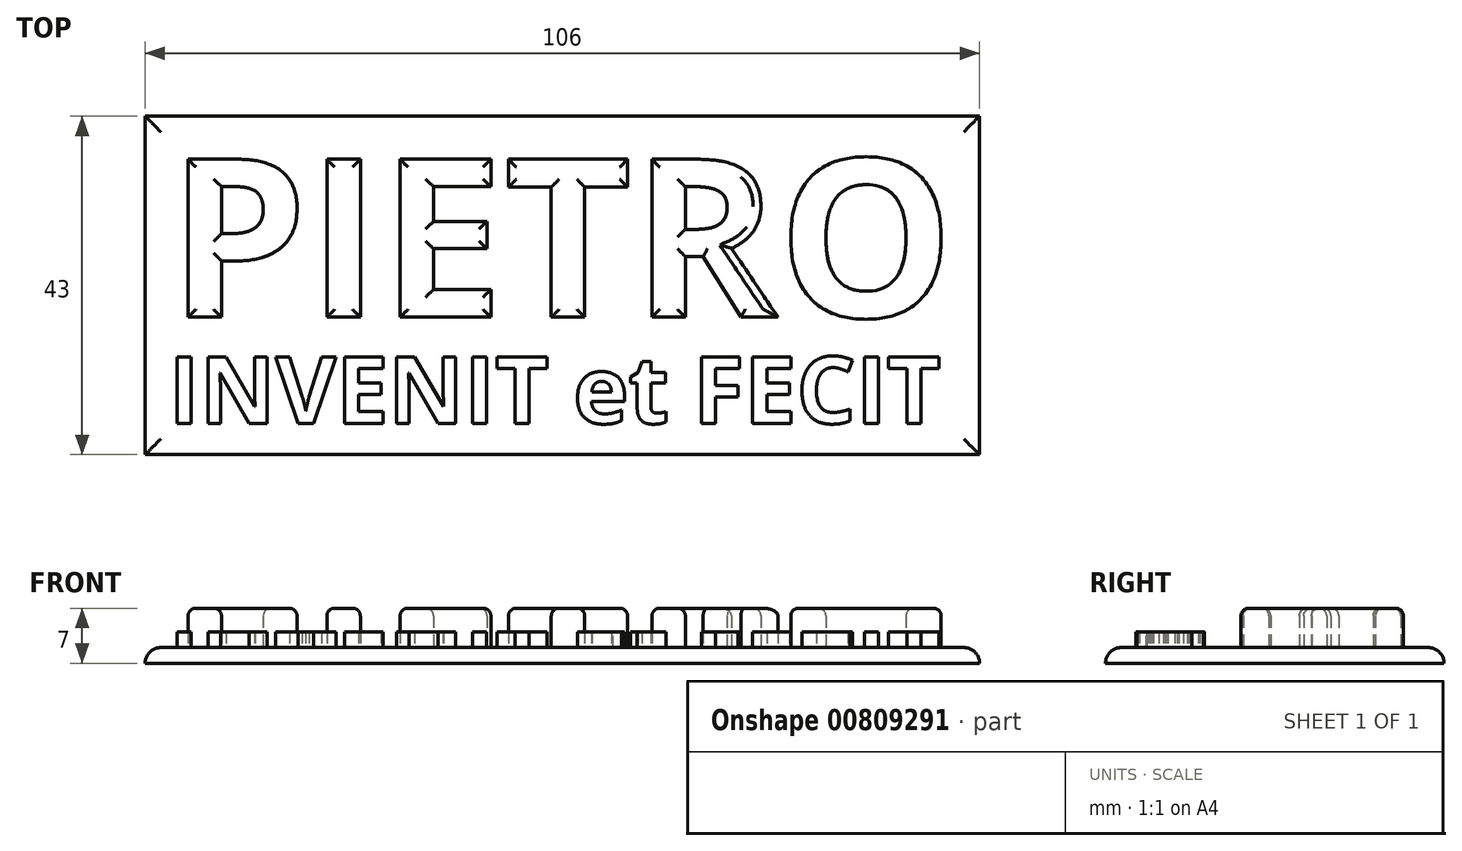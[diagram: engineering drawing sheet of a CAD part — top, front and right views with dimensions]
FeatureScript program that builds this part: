
annotation { "Feature Type Name" : "Feature", "Feature Type Description" : "" }
export const myFeature = defineFeature(function(context is Context, id is Id, definition is map)
    precondition{}
    {
        {
            var Q0;
            Q0=qCreatedBy(makeId("Top.planeOp"),FACE);
            var sketch = newSketch(context, id + "F0", { "sketchPlane" : qUnion([Q0])});
            skText(sketch, "E0", { "text": "PIETRO", "fontName": "OpenSans-Bold.ttf"});
            skText(sketch, "E1", { "text": "INVENIT et FECIT", "fontName": "OpenSans-Bold.ttf"});
            const initialGuessF0  = {"E0": [-0.02736, -0.01022, 1, 0, 0.02022], "E1": [-0.02728, -0.02372, 1, 0, 0.00853]};
            skSetInitialGuess(sketch, initialGuessF0);
            skSolve(sketch);
        }
        {
            var Q0;
            Q0=qCreatedBy(makeId("Top.planeOp"),FACE);
            var sketch = newSketch(context, id + "F1", { "sketchPlane" : qUnion([Q0])});
            skLineSegment(sketch, "E2.bottom", {"start": v(-30.29, 15.3) * mm, "end": v(75.71, 15.3) * mm});
            skLineSegment(sketch, "E2.top", {"start": v(-30.29, -27.7) * mm, "end": v(75.71, -27.7) * mm});
            skLineSegment(sketch, "E2.left", {"start": v(-30.29, 15.3) * mm, "end": v(-30.29, -27.7) * mm});
            skLineSegment(sketch, "E2.right", {"start": v(75.71, 15.3) * mm, "end": v(75.71, -27.7) * mm});
            skSolve(sketch);
        }
        {
            var Q0;
            Q0=makeQuery(id+"F1.imprint","IMPRINT",FACE,{"disambiguationData":[TD([[makeQuery(id+"F1.imprint","IMPRINT",EDGE,{"derivedFrom":sQuery(id+"F1.wireOp",EDGE,"E2.bottom")}),-1.0]])]});
            extrude(context, id + "F2", {"entities" : qUnion([Q0]), "depth" : -2 * mm, "offsetDistance" : 25 * mm});
        }
        {
            var Q0;
            Q0=makeQuery(id+"F0.imprint","IMPRINT",FACE,{"disambiguationData":[TD([[makeQuery(id+"F0.imprint","IMPRINT",EDGE,{"derivedFrom":sQuery(id+"F0.wireOp",EDGE,"E0.sketch_text.stroke-0")}),-1.0]])]});
            var Q1;
            Q1=makeQuery(id+"F0.imprint","IMPRINT",FACE,{"disambiguationData":[TD([[makeQuery(id+"F0.imprint","IMPRINT",EDGE,{"derivedFrom":sQuery(id+"F0.wireOp",EDGE,"E0.sketch_text.stroke-16")}),-1.0]])]});
            var Q2;
            Q2=makeQuery(id+"F0.imprint","IMPRINT",FACE,{"disambiguationData":[TD([[makeQuery(id+"F0.imprint","IMPRINT",EDGE,{"derivedFrom":sQuery(id+"F0.wireOp",EDGE,"E0.sketch_text.stroke-20")}),-1.0]])]});
            var Q3;
            Q3=makeQuery(id+"F0.imprint","IMPRINT",FACE,{"disambiguationData":[TD([[makeQuery(id+"F0.imprint","IMPRINT",EDGE,{"derivedFrom":sQuery(id+"F0.wireOp",EDGE,"E0.sketch_text.stroke-32")}),-1.0]])]});
            var Q4;
            Q4=makeQuery(id+"F0.imprint","IMPRINT",FACE,{"disambiguationData":[TD([[makeQuery(id+"F0.imprint","IMPRINT",EDGE,{"derivedFrom":sQuery(id+"F0.wireOp",EDGE,"E0.sketch_text.stroke-40")}),-1.0]])]});
            var Q5;
            Q5=makeQuery(id+"F0.imprint","IMPRINT",FACE,{"disambiguationData":[TD([[makeQuery(id+"F0.imprint","IMPRINT",EDGE,{"derivedFrom":sQuery(id+"F0.wireOp",EDGE,"E0.sketch_text.stroke-59")}),-1.0]])]});
            extrude(context, id + "F3", {"entities" : qUnion([Q0, Q1, Q2, Q3, Q4, Q5]), "operationType" : NewBodyOperationType.ADD, "depth" : 5 * mm, "offsetDistance" : 25 * mm});
        }
        {
            var Q0;
            Q0=makeQuery(id+"F0.imprint","IMPRINT",FACE,{"disambiguationData":[TD([[makeQuery(id+"F0.imprint","IMPRINT",EDGE,{"derivedFrom":sQuery(id+"F0.wireOp",EDGE,"E1.sketch_text.stroke-0")}),-1.0]])]});
            var Q1;
            Q1=makeQuery(id+"F0.imprint","IMPRINT",FACE,{"disambiguationData":[TD([[makeQuery(id+"F0.imprint","IMPRINT",EDGE,{"derivedFrom":sQuery(id+"F0.wireOp",EDGE,"E1.sketch_text.stroke-4")}),-1.0]])]});
            var Q2;
            Q2=makeQuery(id+"F0.imprint","IMPRINT",FACE,{"disambiguationData":[TD([[makeQuery(id+"F0.imprint","IMPRINT",EDGE,{"derivedFrom":sQuery(id+"F0.wireOp",EDGE,"E1.sketch_text.stroke-18")}),-1.0]])]});
            var Q3;
            Q3=makeQuery(id+"F0.imprint","IMPRINT",FACE,{"disambiguationData":[TD([[makeQuery(id+"F0.imprint","IMPRINT",EDGE,{"derivedFrom":sQuery(id+"F0.wireOp",EDGE,"E1.sketch_text.stroke-28")}),-1.0]])]});
            var Q4;
            Q4=makeQuery(id+"F0.imprint","IMPRINT",FACE,{"disambiguationData":[TD([[makeQuery(id+"F0.imprint","IMPRINT",EDGE,{"derivedFrom":sQuery(id+"F0.wireOp",EDGE,"E1.sketch_text.stroke-40")}),-1.0]])]});
            var Q5;
            Q5=makeQuery(id+"F0.imprint","IMPRINT",FACE,{"disambiguationData":[TD([[makeQuery(id+"F0.imprint","IMPRINT",EDGE,{"derivedFrom":sQuery(id+"F0.wireOp",EDGE,"E1.sketch_text.stroke-54")}),-1.0]])]});
            var Q6;
            Q6=makeQuery(id+"F0.imprint","IMPRINT",FACE,{"disambiguationData":[TD([[makeQuery(id+"F0.imprint","IMPRINT",EDGE,{"derivedFrom":sQuery(id+"F0.wireOp",EDGE,"E1.sketch_text.stroke-58")}),-1.0]])]});
            var Q7;
            Q7=makeQuery(id+"F0.imprint","IMPRINT",FACE,{"disambiguationData":[TD([[makeQuery(id+"F0.imprint","IMPRINT",EDGE,{"derivedFrom":sQuery(id+"F0.wireOp",EDGE,"E1.sketch_text.stroke-66")}),-1.0]])]});
            var Q8;
            Q8=makeQuery(id+"F0.imprint","IMPRINT",FACE,{"disambiguationData":[TD([[makeQuery(id+"F0.imprint","IMPRINT",EDGE,{"derivedFrom":sQuery(id+"F0.wireOp",EDGE,"E1.sketch_text.stroke-78")}),-1.0]])]});
            var Q9;
            Q9=makeQuery(id+"F0.imprint","IMPRINT",FACE,{"disambiguationData":[TD([[makeQuery(id+"F0.imprint","IMPRINT",EDGE,{"derivedFrom":sQuery(id+"F0.wireOp",EDGE,"E1.sketch_text.stroke-86")}),-1.0]])]});
            var Q10;
            Q10=makeQuery(id+"F0.imprint","IMPRINT",FACE,{"disambiguationData":[TD([[makeQuery(id+"F0.imprint","IMPRINT",EDGE,{"derivedFrom":sQuery(id+"F0.wireOp",EDGE,"E1.sketch_text.stroke-96")}),-1.0]])]});
            var Q11;
            Q11=makeQuery(id+"F0.imprint","IMPRINT",FACE,{"disambiguationData":[TD([[makeQuery(id+"F0.imprint","IMPRINT",EDGE,{"derivedFrom":sQuery(id+"F0.wireOp",EDGE,"E1.sketch_text.stroke-108")}),-1.0]])]});
            var Q12;
            Q12=makeQuery(id+"F0.imprint","IMPRINT",FACE,{"disambiguationData":[TD([[makeQuery(id+"F0.imprint","IMPRINT",EDGE,{"derivedFrom":sQuery(id+"F0.wireOp",EDGE,"E1.sketch_text.stroke-123")}),-1.0]])]});
            var Q13;
            Q13=makeQuery(id+"F0.imprint","IMPRINT",FACE,{"disambiguationData":[TD([[makeQuery(id+"F0.imprint","IMPRINT",EDGE,{"derivedFrom":sQuery(id+"F0.wireOp",EDGE,"E1.sketch_text.stroke-127")}),-1.0]])]});
            var Q14;
            Q14=makeQuery(id+"F0.imprint","IMPRINT",FACE,{"disambiguationData":[TD([[makeQuery(id+"F0.imprint","IMPRINT",EDGE,{"derivedFrom":sQuery(id+"F0.wireOp",EDGE,"E1.sketch_text.stroke-141")}),-1.0]])]});
            var Q15;
            Q15=makeQuery(id+"F0.imprint","IMPRINT",FACE,{"disambiguationData":[TD([[makeQuery(id+"F0.imprint","IMPRINT",EDGE,{"derivedFrom":sQuery(id+"F0.wireOp",EDGE,"E1.sketch_text.stroke-145")}),-1.0]])]});
            extrude(context, id + "F4", {"entities" : qUnion([Q0, Q1, Q2, Q3, Q4, Q5, Q6, Q7, Q8, Q9, Q10, Q11, Q12, Q13, Q14, Q15]), "operationType" : NewBodyOperationType.ADD, "depth" : 2 * mm, "offsetDistance" : 25 * mm});
        }
        {
            var Q0;
            Q0=makeQuery(id+"F2.opExtrude","CAP_EDGE",EDGE,{"disambiguationData":[OSD([sQuery(id+"F1.wireOp",EDGE,"E2.right")])],"isStart":true});
            var Q1;
            Q1=makeQuery(id+"F2.opExtrude","CAP_EDGE",EDGE,{"disambiguationData":[OSD([sQuery(id+"F1.wireOp",EDGE,"E2.bottom")])],"isStart":true});
            var Q2;
            Q2=makeQuery(id+"F2.opExtrude","CAP_EDGE",EDGE,{"disambiguationData":[OSD([sQuery(id+"F1.wireOp",EDGE,"E2.top")])],"isStart":true});
            var Q3;
            Q3=makeQuery(id+"F2.opExtrude","CAP_EDGE",EDGE,{"disambiguationData":[OSD([sQuery(id+"F1.wireOp",EDGE,"E2.left")])],"isStart":true});
            fillet(context, id + "F5", {"entities" : qUnion([Q0, Q1, Q2, Q3]), "radius" : 2 * mm, "tangentPropagation" : true, "allowEdgeOverflow" : false});
        }
        {
            var Q0;
            Q0=makeQuery(id+"F3.opExtrude","CAP_FACE",FACE,{"disambiguationData":[OSD([sQuery(id+"F0.wireOp",EDGE,"E0.sketch_text.stroke-0"),sQuery(id+"F0.wireOp",EDGE,"E0.sketch_text.stroke-1"),sQuery(id+"F0.wireOp",EDGE,"E0.sketch_text.stroke-2"),sQuery(id+"F0.wireOp",EDGE,"E0.sketch_text.stroke-3"),sQuery(id+"F0.wireOp",EDGE,"E0.sketch_text.stroke-4"),sQuery(id+"F0.wireOp",EDGE,"E0.sketch_text.stroke-5"),sQuery(id+"F0.wireOp",EDGE,"E0.sketch_text.stroke-6"),sQuery(id+"F0.wireOp",EDGE,"E0.sketch_text.stroke-7"),sQuery(id+"F0.wireOp",EDGE,"E0.sketch_text.stroke-8"),sQuery(id+"F0.wireOp",EDGE,"E0.sketch_text.stroke-9"),sQuery(id+"F0.wireOp",EDGE,"E0.sketch_text.stroke-10"),sQuery(id+"F0.wireOp",EDGE,"E0.sketch_text.stroke-11"),sQuery(id+"F0.wireOp",EDGE,"E0.sketch_text.stroke-12"),sQuery(id+"F0.wireOp",EDGE,"E0.sketch_text.stroke-13"),sQuery(id+"F0.wireOp",EDGE,"E0.sketch_text.stroke-14"),sQuery(id+"F0.wireOp",EDGE,"E0.sketch_text.stroke-15")])],"isStart":false});
            var Q1;
            Q1=makeQuery(id+"F3.opExtrude","CAP_FACE",FACE,{"disambiguationData":[OSD([sQuery(id+"F0.wireOp",EDGE,"E0.sketch_text.stroke-16"),sQuery(id+"F0.wireOp",EDGE,"E0.sketch_text.stroke-17"),sQuery(id+"F0.wireOp",EDGE,"E0.sketch_text.stroke-18"),sQuery(id+"F0.wireOp",EDGE,"E0.sketch_text.stroke-19")])],"isStart":false});
            var Q2;
            Q2=makeQuery(id+"F3.opExtrude","CAP_FACE",FACE,{"disambiguationData":[OSD([sQuery(id+"F0.wireOp",EDGE,"E0.sketch_text.stroke-20"),sQuery(id+"F0.wireOp",EDGE,"E0.sketch_text.stroke-21"),sQuery(id+"F0.wireOp",EDGE,"E0.sketch_text.stroke-22"),sQuery(id+"F0.wireOp",EDGE,"E0.sketch_text.stroke-23"),sQuery(id+"F0.wireOp",EDGE,"E0.sketch_text.stroke-24"),sQuery(id+"F0.wireOp",EDGE,"E0.sketch_text.stroke-25"),sQuery(id+"F0.wireOp",EDGE,"E0.sketch_text.stroke-26"),sQuery(id+"F0.wireOp",EDGE,"E0.sketch_text.stroke-27"),sQuery(id+"F0.wireOp",EDGE,"E0.sketch_text.stroke-28"),sQuery(id+"F0.wireOp",EDGE,"E0.sketch_text.stroke-29"),sQuery(id+"F0.wireOp",EDGE,"E0.sketch_text.stroke-30"),sQuery(id+"F0.wireOp",EDGE,"E0.sketch_text.stroke-31")])],"isStart":false});
            var Q3;
            Q3=makeQuery(id+"F3.opExtrude","CAP_FACE",FACE,{"disambiguationData":[OSD([sQuery(id+"F0.wireOp",EDGE,"E0.sketch_text.stroke-32"),sQuery(id+"F0.wireOp",EDGE,"E0.sketch_text.stroke-33"),sQuery(id+"F0.wireOp",EDGE,"E0.sketch_text.stroke-34"),sQuery(id+"F0.wireOp",EDGE,"E0.sketch_text.stroke-35"),sQuery(id+"F0.wireOp",EDGE,"E0.sketch_text.stroke-36"),sQuery(id+"F0.wireOp",EDGE,"E0.sketch_text.stroke-37"),sQuery(id+"F0.wireOp",EDGE,"E0.sketch_text.stroke-38"),sQuery(id+"F0.wireOp",EDGE,"E0.sketch_text.stroke-39")])],"isStart":false});
            var Q4;
            Q4=makeQuery(id+"F3.opExtrude","CAP_FACE",FACE,{"disambiguationData":[OSD([sQuery(id+"F0.wireOp",EDGE,"E0.sketch_text.stroke-40"),sQuery(id+"F0.wireOp",EDGE,"E0.sketch_text.stroke-41"),sQuery(id+"F0.wireOp",EDGE,"E0.sketch_text.stroke-42"),sQuery(id+"F0.wireOp",EDGE,"E0.sketch_text.stroke-43"),sQuery(id+"F0.wireOp",EDGE,"E0.sketch_text.stroke-44"),sQuery(id+"F0.wireOp",EDGE,"E0.sketch_text.stroke-45"),sQuery(id+"F0.wireOp",EDGE,"E0.sketch_text.stroke-46"),sQuery(id+"F0.wireOp",EDGE,"E0.sketch_text.stroke-47"),sQuery(id+"F0.wireOp",EDGE,"E0.sketch_text.stroke-48"),sQuery(id+"F0.wireOp",EDGE,"E0.sketch_text.stroke-49"),sQuery(id+"F0.wireOp",EDGE,"E0.sketch_text.stroke-50"),sQuery(id+"F0.wireOp",EDGE,"E0.sketch_text.stroke-51"),sQuery(id+"F0.wireOp",EDGE,"E0.sketch_text.stroke-52"),sQuery(id+"F0.wireOp",EDGE,"E0.sketch_text.stroke-53"),sQuery(id+"F0.wireOp",EDGE,"E0.sketch_text.stroke-54"),sQuery(id+"F0.wireOp",EDGE,"E0.sketch_text.stroke-55"),sQuery(id+"F0.wireOp",EDGE,"E0.sketch_text.stroke-56"),sQuery(id+"F0.wireOp",EDGE,"E0.sketch_text.stroke-57"),sQuery(id+"F0.wireOp",EDGE,"E0.sketch_text.stroke-58")])],"isStart":false});
            var Q5;
            Q5=makeQuery(id+"F3.opExtrude","CAP_FACE",FACE,{"disambiguationData":[OSD([sQuery(id+"F0.wireOp",EDGE,"E0.sketch_text.stroke-59"),sQuery(id+"F0.wireOp",EDGE,"E0.sketch_text.stroke-60"),sQuery(id+"F0.wireOp",EDGE,"E0.sketch_text.stroke-61"),sQuery(id+"F0.wireOp",EDGE,"E0.sketch_text.stroke-62"),sQuery(id+"F0.wireOp",EDGE,"E0.sketch_text.stroke-63"),sQuery(id+"F0.wireOp",EDGE,"E0.sketch_text.stroke-64"),sQuery(id+"F0.wireOp",EDGE,"E0.sketch_text.stroke-65"),sQuery(id+"F0.wireOp",EDGE,"E0.sketch_text.stroke-66"),sQuery(id+"F0.wireOp",EDGE,"E0.sketch_text.stroke-67"),sQuery(id+"F0.wireOp",EDGE,"E0.sketch_text.stroke-68"),sQuery(id+"F0.wireOp",EDGE,"E0.sketch_text.stroke-69"),sQuery(id+"F0.wireOp",EDGE,"E0.sketch_text.stroke-70"),sQuery(id+"F0.wireOp",EDGE,"E0.sketch_text.stroke-71"),sQuery(id+"F0.wireOp",EDGE,"E0.sketch_text.stroke-72")])],"isStart":false});
            fillet(context, id + "F6", {"entities" : qUnion([Q0, Q1, Q2, Q3, Q4, Q5]), "radius" : 1 * mm, "tangentPropagation" : true, "allowEdgeOverflow" : false});
        }
    });
